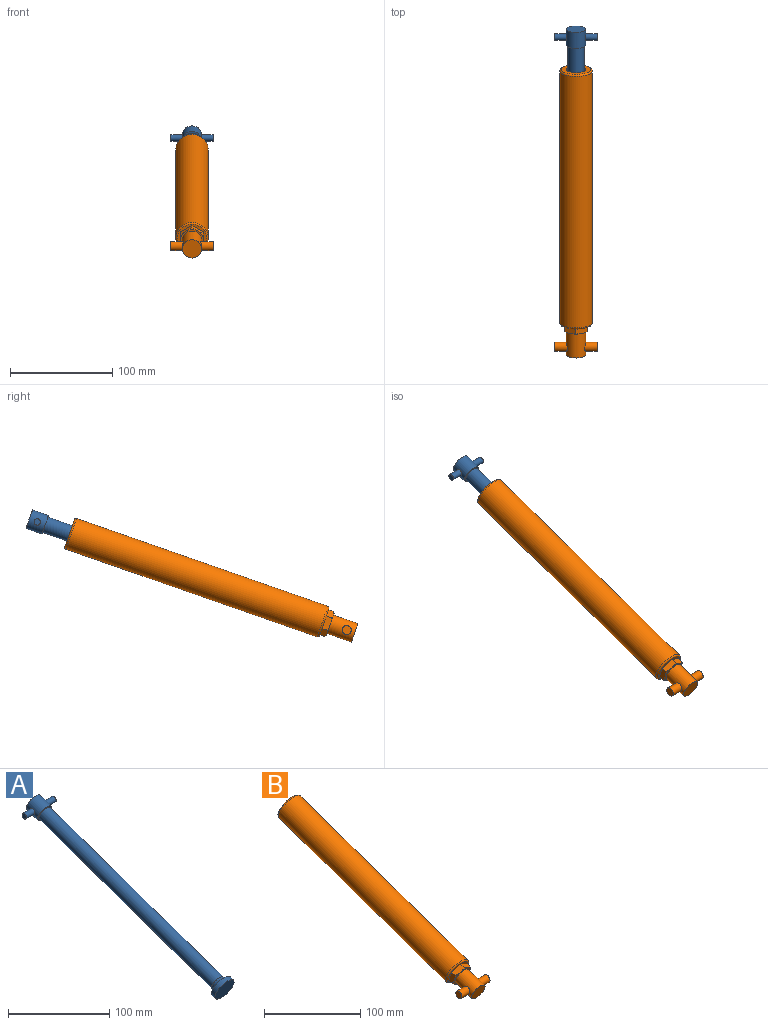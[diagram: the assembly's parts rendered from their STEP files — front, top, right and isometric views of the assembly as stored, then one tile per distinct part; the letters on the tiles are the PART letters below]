
ASSEMBLY  parts=2 mates=1
PART A: 11 faces, bbox 41.4x273.8x114.1 mm
  f0: cylinder r=9.53mm len=23.43mm, axis (0,-0.94,-0.33), area 923.7mm2, adj f1,f2,f8,f9
  f1: plane 19.05x17.98mm, normal (0,0.94,0.33), area 285mm2, adj f0
  f2: plane 19.05x17.98mm, normal (0,-0.94,-0.33), area 90.2mm2, adj f0,f3
  f3: cylinder r=7.87mm len=246.47mm, axis (0,0.94,0.33), area 12644.2mm2, adj f2,f6
  f4: cylinder r=12.7mm len=25.65mm, axis (0,0.94,0.33), area 405.4mm2, adj f5,f6
  f5: plane 25.4x23.98mm, normal (0,-0.94,-0.33), area 506.7mm2, adj f4
  f6: torus R=12.95mm, axis (0,-0.94,-0.33), area 466.9mm2, adj f3,f4
  f7: plane 6.35x6.35mm, normal (-1,0,0), area 31.7mm2, adj f8
  f8: cylinder r=3.17mm len=11.72mm, axis (-1,0,0), area 228.3mm2, adj f0,f7
  f9: cylinder r=3.17mm len=11.72mm, axis (-1,0,0), area 228.3mm2, adj f0,f10
  f10: plane 6.35x6.35mm, normal (1,0,0), area 31.7mm2, adj f9
PART B: 29 faces, bbox 41.4x287.3x122.2 mm
  f0: plane 28.58x26.98mm, normal (0,0.94,0.33), area 360.1mm2, adj f7,f27
  f1: cylinder r=15.88mm len=256.54mm, axis (0,-0.94,-0.33), area 25998.4mm2, adj f27,f28
  f2: plane 28.58x26.98mm, normal (0,-0.94,-0.33), area 208.6mm2, adj f8,f9,f10,f11,f12,f13,f28
  f3: cylinder r=7.87mm len=15.75mm, axis (0,0.94,0.33), area 78.5mm2, adj f4,f7
  f4: plane 25.4x23.98mm, normal (0,-0.94,-0.33), area 311.9mm2, adj f3,f5
  f5: cylinder r=12.7mm len=251.44mm, axis (0,-0.94,-0.33), area 20545.3mm2, adj f4,f6
  f6: plane 25.4x23.98mm, normal (0,0.94,0.33), area 506.7mm2, adj f5
  f7: cone r=9.46mm half-angle=45deg, axis (0,0.94,0.33), area 122.3mm2, adj f0,f3
  f8: plane 13.97x9.36mm, normal (-1,0,0), area 78mm2, adj f2,f9,f13,f14,f18,f22
  f9: plane 11.18x7.87mm, normal (-0.5,-0.29,0.82), area 78mm2, adj f2,f8,f10,f14,f21,f22
  f10: plane 11.18x7.87mm, normal (0.5,-0.29,0.82), area 78mm2, adj f2,f9,f11,f14,f20,f21
  f11: plane 13.97x9.35mm, normal (1,0,0), area 78mm2, adj f2,f10,f12,f14,f19,f20
  f12: plane 11.18x7.87mm, normal (0.5,0.29,-0.82), area 78mm2, adj f2,f11,f13,f14,f17,f19
  f13: plane 11.18x7.87mm, normal (-0.5,0.29,-0.82), area 78mm2, adj f2,f8,f12,f14,f17,f18
  f14: plane 22.35x21.25mm, normal (0,-0.94,-0.33), area 112mm2, adj f8,f9,f10,f11,f12,f13,f15,f17
  f15: cylinder r=9.53mm len=30.26mm, axis (0,0.94,0.33), area 1392.6mm2, adj f14,f16,f24,f25
  f16: plane 19.05x17.98mm, normal (0,-0.94,-0.33), area 285mm2, adj f15
  f17: cone r=12.9mm half-angle=60deg, axis (0,0.94,0.33), area 6.9mm2, adj f12,f13,f14
  f18: cone r=12.9mm half-angle=60deg, axis (0,0.94,0.33), area 6.9mm2, adj f8,f13,f14
  f19: cone r=12.9mm half-angle=60deg, axis (0,0.94,0.33), area 6.9mm2, adj f11,f12,f14
  f20: cone r=12.9mm half-angle=60deg, axis (0,0.94,0.33), area 6.9mm2, adj f10,f11,f14
  f21: cone r=12.9mm half-angle=60deg, axis (0,0.94,0.33), area 6.9mm2, adj f9,f10,f14
  f22: cone r=12.9mm half-angle=60deg, axis (0,0.94,0.33), area 6.9mm2, adj f8,f9,f14
  f23: plane 8.89x8.89mm, normal (-1,0,0), area 62.1mm2, adj f24
  f24: cylinder r=4.45mm len=12.28mm, axis (-1,0,0), area 327.3mm2, adj f15,f23
  f25: cylinder r=4.45mm len=12.28mm, axis (-1,0,0), area 327.3mm2, adj f15,f26
  f26: plane 8.89x8.89mm, normal (1,0,0), area 62.1mm2, adj f25
  f27: torus R=14.29mm, axis (0,0.94,0.33), area 239.7mm2, adj f0,f1
  f28: torus R=14.29mm, axis (0,0.94,0.33), area 239.7mm2, adj f1,f2
PLACE A t=(-426.44,839.14,-354.54)mm
PLACE B rot(axis=(0,-0.96,-0.29),0deg) t=(-426.44,839.14,-354.54)mm
MATE slider A.f6 <-> B.f15  axis (0,-0.94,-0.33) through (-426.44,-136.15,47.12)mm
